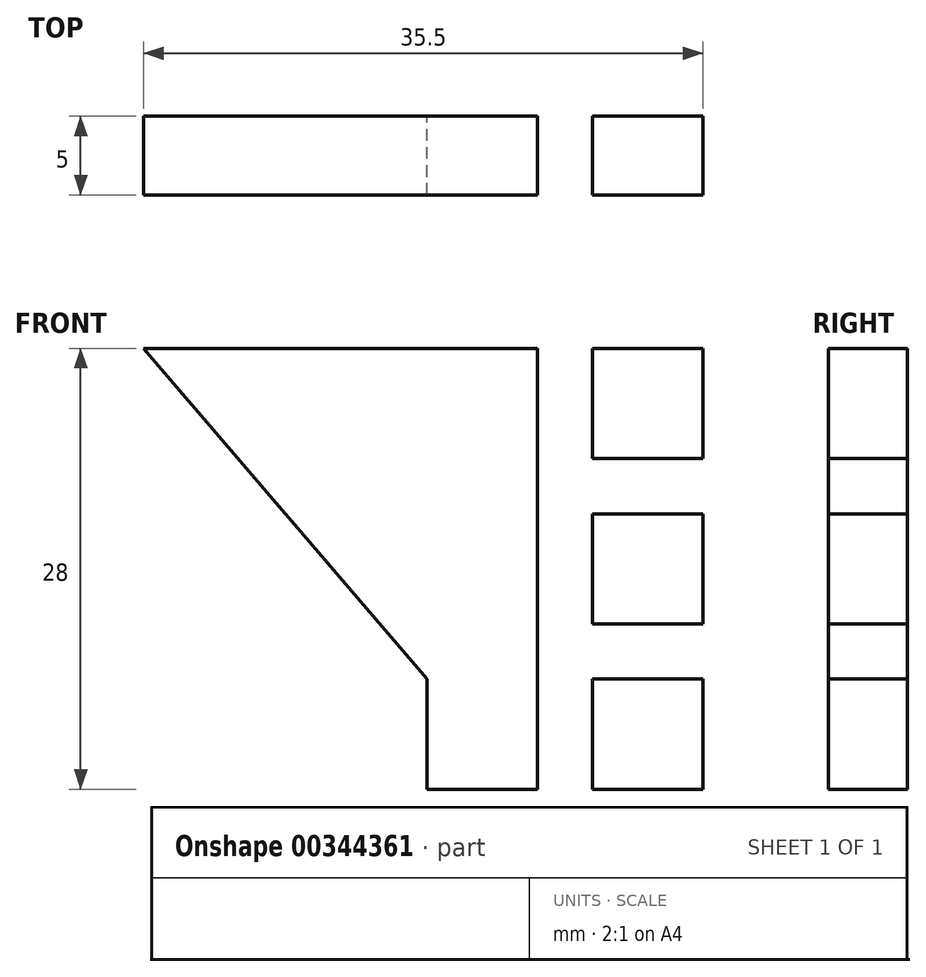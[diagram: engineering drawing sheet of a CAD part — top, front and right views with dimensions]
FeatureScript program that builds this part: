
annotation { "Feature Type Name" : "Feature", "Feature Type Description" : "" }
export const myFeature = defineFeature(function(context is Context, id is Id, definition is map)
    precondition{}
    {
        {
            var Q0;
            Q0=qCreatedBy(makeId("Front.planeOp"),FACE);
            var sketch = newSketch(context, id + "F0", { "sketchPlane" : qUnion([Q0])});
            skLineSegment(sketch, "E0", {"start": v(-25, 28) * mm, "end": v(0, 28) * mm});
            skLineSegment(sketch, "E1", {"start": v(0, 28) * mm, "end": v(0, 0) * mm});
            skLineSegment(sketch, "E2", {"start": v(0, 0) * mm, "end": v(-7, 0) * mm});
            skLineSegment(sketch, "E3", {"start": v(-7, 0) * mm, "end": v(-7, 7) * mm});
            skLineSegment(sketch, "E4", {"start": v(-7, 7) * mm, "end": v(-25, 28) * mm});
            skLineSegment(sketch, "E5.bottom", {"start": v(3.5, 28) * mm, "end": v(10.5, 28) * mm});
            skLineSegment(sketch, "E5.top", {"start": v(3.5, 21) * mm, "end": v(10.5, 21) * mm});
            skLineSegment(sketch, "E5.left", {"start": v(3.5, 28) * mm, "end": v(3.5, 21) * mm});
            skLineSegment(sketch, "E5.right", {"start": v(10.5, 28) * mm, "end": v(10.5, 21) * mm});
            skLineSegment(sketch, "E6.bottom", {"start": v(3.5, 17.5) * mm, "end": v(10.5, 17.5) * mm});
            skLineSegment(sketch, "E6.top", {"start": v(3.5, 10.5) * mm, "end": v(10.5, 10.5) * mm});
            skLineSegment(sketch, "E6.left", {"start": v(3.5, 17.5) * mm, "end": v(3.5, 10.5) * mm});
            skLineSegment(sketch, "E6.right", {"start": v(10.5, 17.5) * mm, "end": v(10.5, 10.5) * mm});
            skLineSegment(sketch, "E7.bottom", {"start": v(3.5, 7) * mm, "end": v(10.5, 7) * mm});
            skLineSegment(sketch, "E7.top", {"start": v(3.5, 0) * mm, "end": v(10.5, 0) * mm});
            skLineSegment(sketch, "E7.left", {"start": v(3.5, 7) * mm, "end": v(3.5, 0) * mm});
            skLineSegment(sketch, "E7.right", {"start": v(10.5, 7) * mm, "end": v(10.5, 0) * mm});
            skSolve(sketch);
        }
        {
            var Q0;
            Q0=makeQuery(id+"F0.imprint","IMPRINT",FACE,{"disambiguationData":[TD([[makeQuery(id+"F0.imprint","IMPRINT",EDGE,{"derivedFrom":sQuery(id+"F0.wireOp",EDGE,"E0")}),-1.0]])]});
            var Q1;
            Q1=makeQuery(id+"F0.imprint","IMPRINT",FACE,{"disambiguationData":[TD([[makeQuery(id+"F0.imprint","IMPRINT",EDGE,{"derivedFrom":sQuery(id+"F0.wireOp",EDGE,"E5.bottom")}),-1.0]])]});
            var Q2;
            Q2=makeQuery(id+"F0.imprint","IMPRINT",FACE,{"disambiguationData":[TD([[makeQuery(id+"F0.imprint","IMPRINT",EDGE,{"derivedFrom":sQuery(id+"F0.wireOp",EDGE,"E6.bottom")}),-1.0]])]});
            var Q3;
            Q3=makeQuery(id+"F0.imprint","IMPRINT",FACE,{"disambiguationData":[TD([[makeQuery(id+"F0.imprint","IMPRINT",EDGE,{"derivedFrom":sQuery(id+"F0.wireOp",EDGE,"E7.bottom")}),-1.0]])]});
            extrude(context, id + "F1", {"entities" : qUnion([Q0, Q1, Q2, Q3]), "depth" : 5 * mm});
        }
    });
